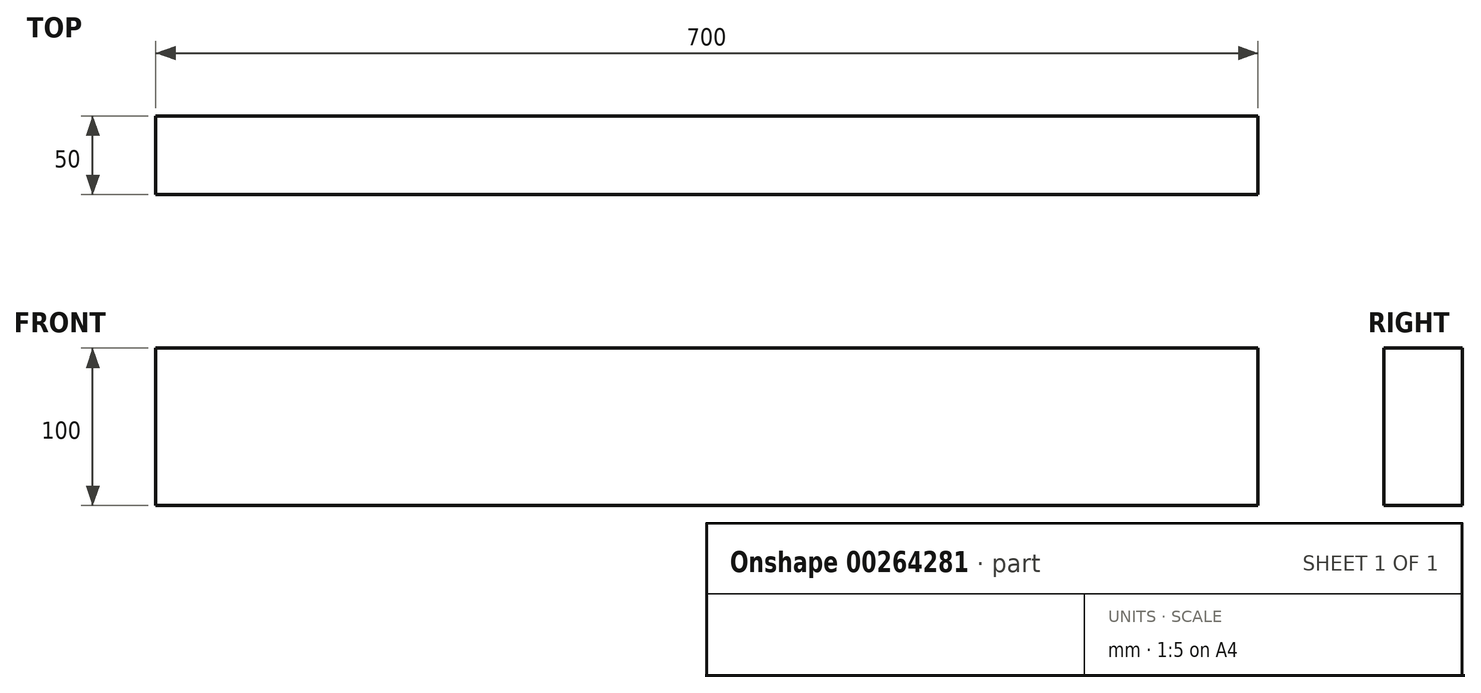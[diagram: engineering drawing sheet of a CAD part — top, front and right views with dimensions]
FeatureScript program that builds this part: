
annotation { "Feature Type Name" : "Feature", "Feature Type Description" : "" }
export const myFeature = defineFeature(function(context is Context, id is Id, definition is map)
    precondition{}
    {
        {
            var Q0;
            Q0=qCreatedBy(makeId("Front.planeOp"),FACE);
            var sketch = newSketch(context, id + "F0", { "sketchPlane" : qUnion([Q0])});
            skLineSegment(sketch, "E0.bottom", {"start": v(-350, 50) * mm, "end": v(350, 50) * mm});
            skLineSegment(sketch, "E0.top", {"start": v(-350, -50) * mm, "end": v(350, -50) * mm});
            skLineSegment(sketch, "E0.left", {"start": v(-350, 50) * mm, "end": v(-350, -50) * mm});
            skLineSegment(sketch, "E0.right", {"start": v(350, 50) * mm, "end": v(350, -50) * mm});
            skLineSegment(sketch, "E1", {"start": v(-350, 0) * mm, "end": v(350, 0) * mm, "construction": true});
            skLineSegment(sketch, "E2", {"start": v(0, 50) * mm, "end": v(0, -50) * mm, "construction": true});
            skSolve(sketch);
        }
        {
            var Q0;
            Q0=makeQuery(id+"F0.imprint","IMPRINT",FACE,{"disambiguationData":[TD([[makeQuery(id+"F0.imprint","IMPRINT",EDGE,{"derivedFrom":sQuery(id+"F0.wireOp",EDGE,"E0.bottom")}),-1.0]])]});
            extrude(context, id + "F1", {"entities" : qUnion([Q0]), "endBound" : BoundingType.SYMMETRIC, "depth" : 50 * mm});
        }
    });
